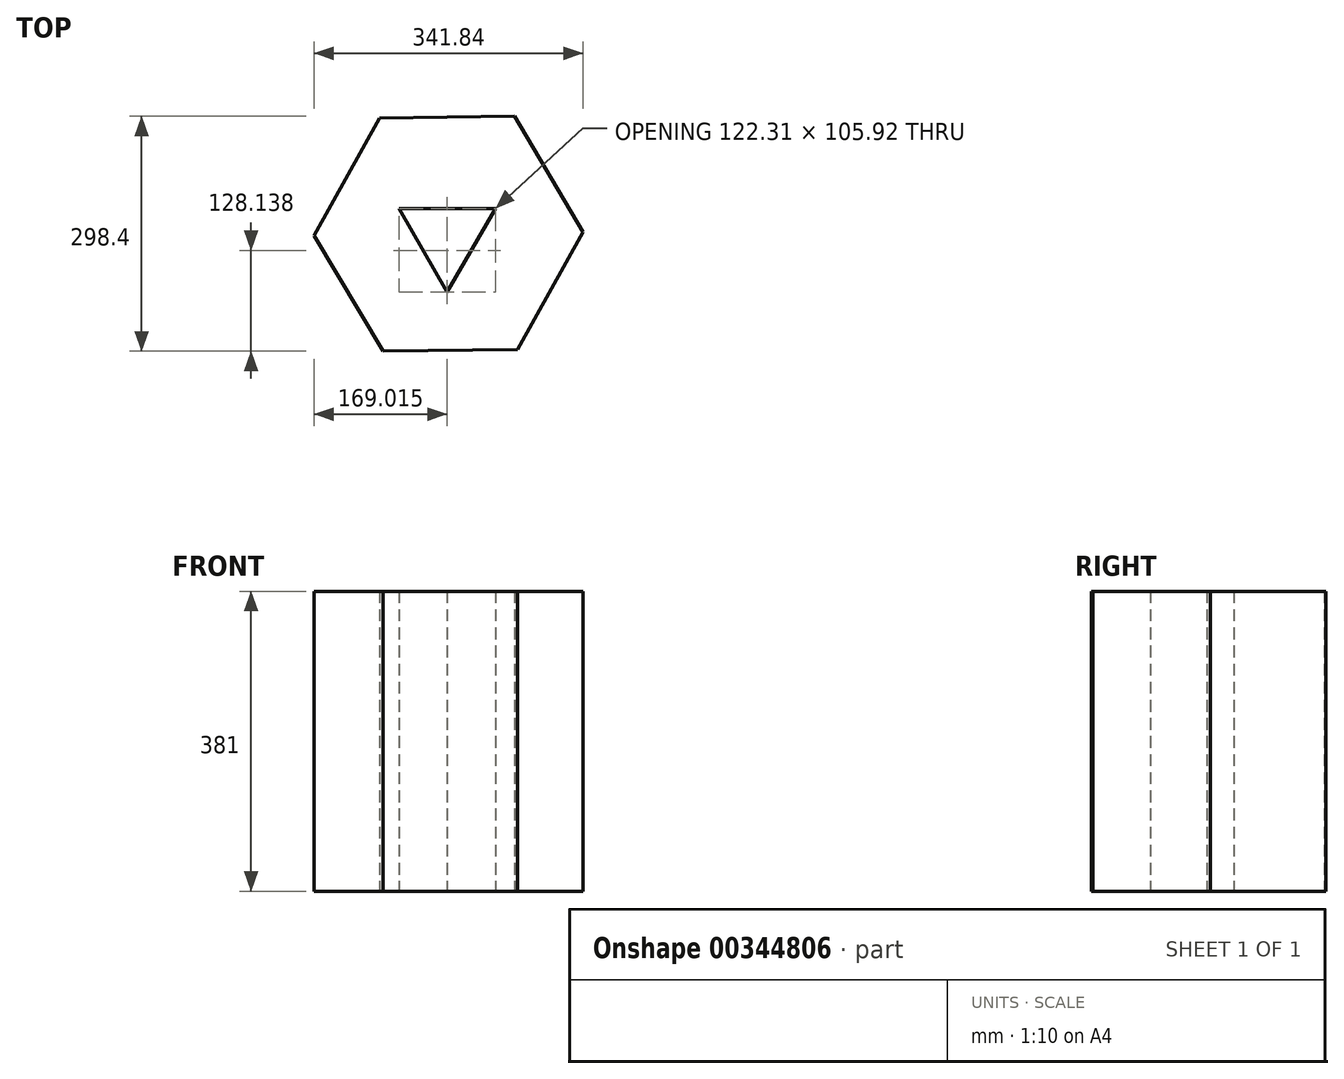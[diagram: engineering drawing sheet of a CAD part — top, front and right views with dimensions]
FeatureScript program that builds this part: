
annotation { "Feature Type Name" : "Feature", "Feature Type Description" : "" }
export const myFeature = defineFeature(function(context is Context, id is Id, definition is map)
    precondition{}
    {
        {
            var Q0;
            Q0=qCreatedBy(makeId("Top.planeOp"),FACE);
            var sketch = newSketch(context, id + "F0", { "sketchPlane" : qUnion([Q0])});
            skLineSegment(sketch, "E0.0", {"start": v(207.52, 371.2) * mm, "end": v(425.3, -0.9) * mm});
            skLineSegment(sketch, "E0.1", {"start": v(425.3, -0.9) * mm, "end": v(217.72, -365.32) * mm});
            skLineSegment(sketch, "E0.2", {"start": v(217.72, -365.32) * mm, "end": v(-207.52, -371.2) * mm});
            skLineSegment(sketch, "E0.3", {"start": v(-207.52, -371.2) * mm, "end": v(-425.24, -5.89) * mm});
            skLineSegment(sketch, "E0.4", {"start": v(-425.24, -5.89) * mm, "end": v(-217.72, 365.32) * mm});
            skLineSegment(sketch, "E0.5", {"start": v(-217.72, 365.32) * mm, "end": v(207.52, 371.2) * mm});
            skLineSegment(sketch, "E1", {"start": v(-207.52, -371.2) * mm, "end": v(-83.4, -149.2) * mm});
            skLineSegment(sketch, "E2", {"start": v(-425.24, -5.89) * mm, "end": v(-169.71, -4.39) * mm});
            skLineSegment(sketch, "E3", {"start": v(217.72, -365.32) * mm, "end": v(87.5, -146.84) * mm});
            skLineSegment(sketch, "E4.0", {"start": v(83.4, 149.2) * mm, "end": v(170.92, 2.37) * mm});
            skLineSegment(sketch, "E4.1", {"start": v(170.92, 2.37) * mm, "end": v(87.5, -146.84) * mm});
            skLineSegment(sketch, "E4.2", {"start": v(87.5, -146.84) * mm, "end": v(-83.4, -149.2) * mm});
            skLineSegment(sketch, "E4.3", {"start": v(-83.4, -149.2) * mm, "end": v(-170.92, -2.37) * mm});
            skLineSegment(sketch, "E4.4", {"start": v(-170.92, -2.37) * mm, "end": v(-87.5, 146.84) * mm});
            skLineSegment(sketch, "E4.5", {"start": v(-87.5, 146.84) * mm, "end": v(83.4, 149.2) * mm});
            skLineSegment(sketch, "E5.0", {"start": v(0, 148.05) * mm, "end": v(128.21, -74.02) * mm});
            skLineSegment(sketch, "E5.1", {"start": v(128.21, -74.02) * mm, "end": v(-128.21, -74.02) * mm});
            skLineSegment(sketch, "E5.2", {"start": v(-128.21, -74.02) * mm, "end": v(0, 148.05) * mm});
            skLineSegment(sketch, "E6.trimOffspring", {"start": v(83.4, 149.2) * mm, "end": v(207.52, 371.2) * mm});
            skLineSegment(sketch, "E7.trimOffspring", {"start": v(-87.5, 146.84) * mm, "end": v(-217.72, 365.32) * mm});
            skLineSegment(sketch, "E8.trimOffspring", {"start": v(2.02, -3.38) * mm, "end": v(0, 0) * mm});
            skLineSegment(sketch, "E9.trimOffspring", {"start": v(-1.9, -3.4) * mm, "end": v(0, 0) * mm});
            skLineSegment(sketch, "E10.trimOffspring", {"start": v(-1.9, -3.4) * mm, "end": v(2.02, -3.38) * mm});
            skLineSegment(sketch, "E11.trimOffspring", {"start": v(168.25, -2.41) * mm, "end": v(425.3, -0.9) * mm});
            skLineSegment(sketch, "E12.0", {"start": v(-1.9, -74.02) * mm, "end": v(-63.06, 31.9) * mm});
            skLineSegment(sketch, "E12.1", {"start": v(-63.06, 31.9) * mm, "end": v(59.25, 31.9) * mm});
            skLineSegment(sketch, "E12.2", {"start": v(59.25, 31.9) * mm, "end": v(-1.9, -74.02) * mm});
            skPoint(sketch, "E13", {"position": v(316.41, 185.15) * mm});
            skPoint(sketch, "E14", {"position": v(321.5, -183.11) * mm});
            skPoint(sketch, "E15", {"position": v(5.1, -368.26) * mm});
            skPoint(sketch, "E16.positionSnap0", {"position": v(-5.1, 368.26) * mm});
            skPoint(sketch, "E17", {"position": v(-321.48, 179.72) * mm});
            skPoint(sketch, "E18", {"position": v(-316.38, -188.55) * mm});
            skLineSegment(sketch, "E19", {"start": v(-87.5, 146.84) * mm, "end": v(-5.1, 368.26) * mm});
            skLineSegment(sketch, "E20", {"start": v(83.4, 149.2) * mm, "end": v(-5.1, 368.26) * mm});
            skLineSegment(sketch, "E21", {"start": v(83.4, 149.2) * mm, "end": v(316.41, 185.15) * mm});
            skLineSegment(sketch, "E22", {"start": v(316.41, 185.15) * mm, "end": v(170.92, 2.37) * mm});
            skLineSegment(sketch, "E23", {"start": v(170.92, 2.37) * mm, "end": v(321.5, -183.11) * mm});
            skLineSegment(sketch, "E24", {"start": v(321.5, -183.11) * mm, "end": v(87.5, -146.84) * mm});
            skLineSegment(sketch, "E25", {"start": v(-83.4, -149.2) * mm, "end": v(5.1, -368.26) * mm});
            skLineSegment(sketch, "E26", {"start": v(87.5, -146.84) * mm, "end": v(5.1, -368.26) * mm});
            skLineSegment(sketch, "E27", {"start": v(-169.71, -4.39) * mm, "end": v(-316.38, -188.55) * mm});
            skLineSegment(sketch, "E28", {"start": v(-316.38, -188.55) * mm, "end": v(-83.4, -149.2) * mm});
            skLineSegment(sketch, "E29", {"start": v(-321.48, 179.72) * mm, "end": v(-169.71, -4.39) * mm});
            skLineSegment(sketch, "E30", {"start": v(-321.48, 179.72) * mm, "end": v(-87.5, 146.84) * mm});
            skSolve(sketch);
        }
        {
            var Q0;
            {var subQ3=sQuery(id+"F0.wireOp",EDGE,"E4.0");Q0=makeQuery(id+"F0.imprint","IMPRINT",FACE,{"disambiguationData":[TD([[makeQuery(id+"F0.imprint","IMPRINT",EDGE,{"derivedFrom":subQ3}),-1.0]])]});}
            var Q1;
            {var subQ5=sQuery(id+"F0.wireOp",EDGE,"E4.2");Q1=makeQuery(id+"F0.imprint","IMPRINT",FACE,{"disambiguationData":[TD([[makeQuery(id+"F0.imprint","IMPRINT",EDGE,{"derivedFrom":subQ5}),-1.0]])]});}
            var Q2;
            {var subQ5=sQuery(id+"F0.wireOp",EDGE,"E5.0");Q2=makeQuery(id+"F0.imprint","IMPRINT",FACE,{"disambiguationData":[TD([[makeQuery(id+"F0.imprint","IMPRINT",EDGE,{"derivedFrom":subQ5}),-1.0]])]});}
            var Q3;
            {var subQ1=sQuery(id+"F0.wireOp",EDGE,"E4.4");Q3=makeQuery(id+"F0.imprint","IMPRINT",FACE,{"disambiguationData":[TD([[makeQuery(id+"F0.imprint","IMPRINT",EDGE,{"derivedFrom":subQ1}),-1.0]])]});}
            var Q4;
            Q4=sQuery(id+"F0.wireOp",EDGE,"E4.0");
            var Q5;
            Q5=sQuery(id+"F0.wireOp",EDGE,"E4.1");
            var Q6;
            Q6=sQuery(id+"F0.wireOp",EDGE,"E4.5");
            var Q7;
            Q7=sQuery(id+"F0.wireOp",EDGE,"E4.4");
            var Q8;
            Q8=sQuery(id+"F0.wireOp",EDGE,"E4.3");
            var Q9;
            Q9=sQuery(id+"F0.wireOp",EDGE,"E4.2");
            extrude(context, id + "F1", {"entities" : qUnion([Q0, Q1, Q2, Q3]), "surfaceEntities" : qUnion([Q4, Q5, Q6, Q7, Q8, Q9]), "depth" : 381 * mm});
        }
        {
            var Q0;
            Q0=makeQuery(id+"F1.opExtrude","CAP_EDGE",EDGE,{"disambiguationData":[OSD([sQuery(id+"F0.wireOp",EDGE,"E4.2")])],"isStart":false});
            cPoint(context, id + "F2", {"entities" : qUnion([Q0]), "parameter" : 0.5});
        }
        {
            var Q0;
            Q0=sQuery(id+"F0.wireOp",EDGE,"E0.2");
            var Q1;
            Q1 = qCreatedBy(id + "F2" ,VERTEX);
            cPlane(context, id + "F3", {"entities" : qUnion([Q0, Q1]), "cplaneType" : CPlaneType.LINE_ANGLE, "offset" : 25.4 * mm, "angle" : 0 * degree, "width" : 152.4 * mm, "height" : 152.4 * mm});
        }
    });
